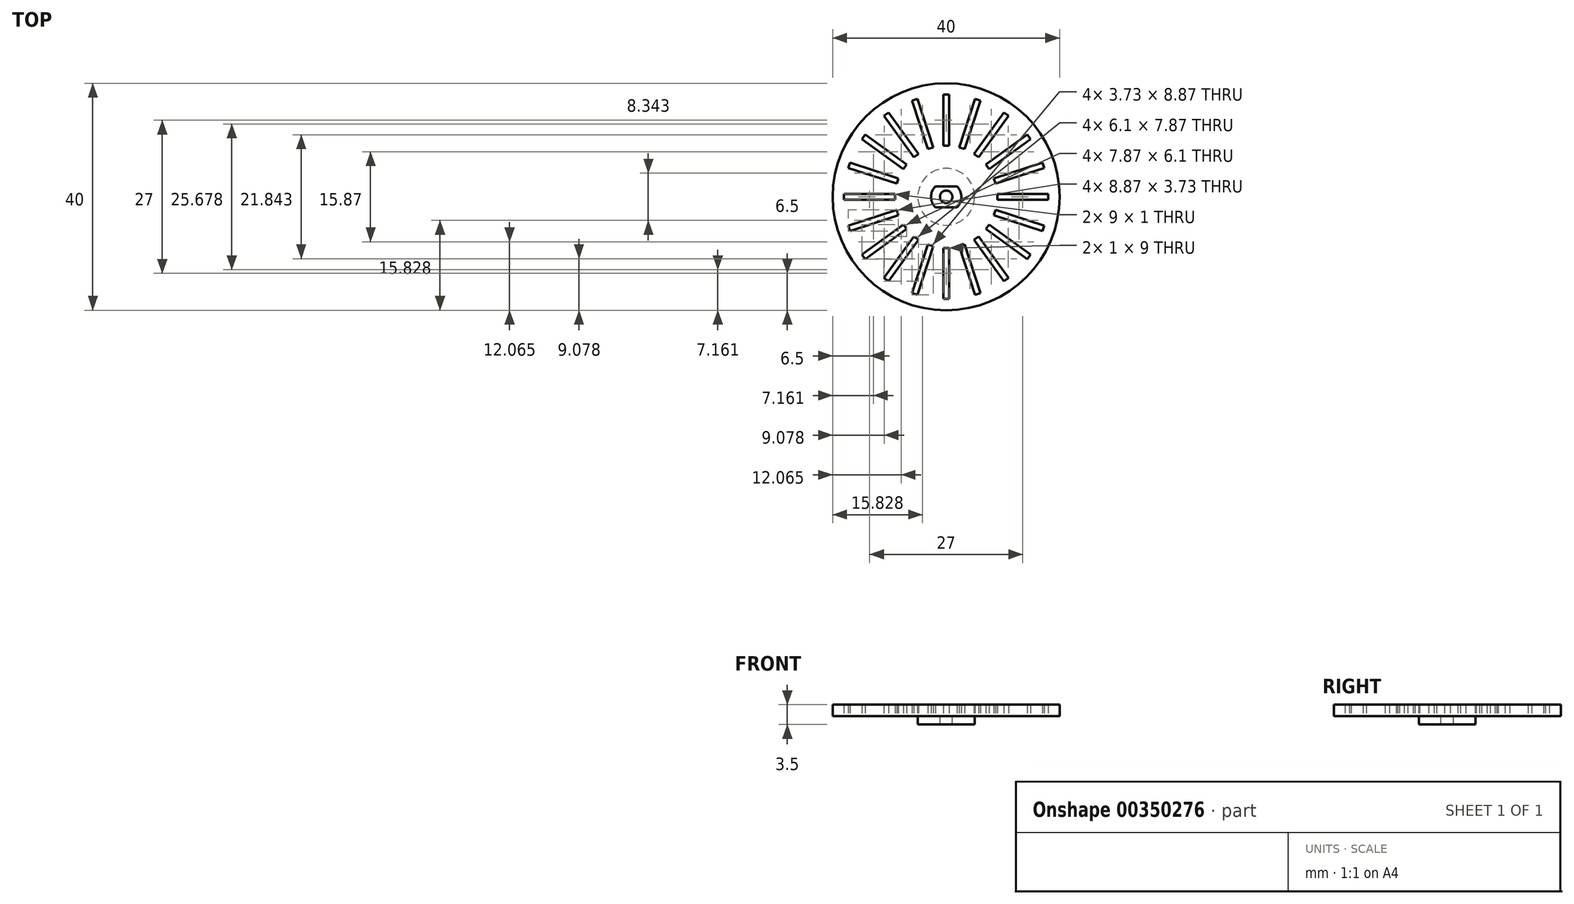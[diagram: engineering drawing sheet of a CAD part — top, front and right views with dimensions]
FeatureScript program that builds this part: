
annotation { "Feature Type Name" : "Feature", "Feature Type Description" : "" }
export const myFeature = defineFeature(function(context is Context, id is Id, definition is map)
    precondition{}
    {
        {
            var Q0;
            Q0=qCreatedBy(makeId("Top.planeOp"),FACE);
            var sketch = newSketch(context, id + "F0", { "sketchPlane" : qUnion([Q0])});
            skCircle(sketch, "E0", {"center": v(0, 0) * mm, "radius": 20 * mm});
            skArc(sketch, "E1", {"start": v(-1.9, 1.86) * mm, "mid": v(-2.67, 0) * mm, "end": v(-1.9, -1.86) * mm});
            skLineSegment(sketch, "E2.MirrorCS", {"start": v(-1.9, -1.86) * mm, "end": v(1.9, -1.86) * mm});
            skArc(sketch, "E3.trimOffspring", {"start": v(1.9, -1.86) * mm, "mid": v(2.67, 0) * mm, "end": v(1.9, 1.86) * mm});
            skLineSegment(sketch, "E4.MirrorCS", {"start": v(-1.9, 1.86) * mm, "end": v(1.9, 1.86) * mm});
            skLineSegment(sketch, "E5", {"start": v(0, -9) * mm, "end": v(-0.5, -9) * mm});
            skLineSegment(sketch, "E6", {"start": v(-0.5, -9) * mm, "end": v(-0.5, -18) * mm});
            skLineSegment(sketch, "E7", {"start": v(-0.5, -18) * mm, "end": v(0, -18) * mm});
            skLineSegment(sketch, "E8.MirrorCS", {"start": v(0.5, -9) * mm, "end": v(0.5, -18) * mm});
            skLineSegment(sketch, "E9", {"start": v(0, -9) * mm, "end": v(0.5, -9) * mm});
            skLineSegment(sketch, "E10", {"start": v(0, -18) * mm, "end": v(0.5, -18) * mm});
            skLineSegment(sketch, "E11.1.0", {"start": v(2.3, -8.71) * mm, "end": v(5.09, -17.27) * mm});
            skLineSegment(sketch, "E11.1.1", {"start": v(3.26, -8.4) * mm, "end": v(6.04, -16.96) * mm});
            skLineSegment(sketch, "E11.1.2", {"start": v(5.09, -17.27) * mm, "end": v(5.56, -17.12) * mm});
            skLineSegment(sketch, "E11.1.3", {"start": v(2.78, -8.56) * mm, "end": v(3.26, -8.4) * mm});
            skLineSegment(sketch, "E11.1.4", {"start": v(5.56, -17.12) * mm, "end": v(6.04, -16.96) * mm});
            skLineSegment(sketch, "E11.1.5", {"start": v(2.78, -8.56) * mm, "end": v(2.3, -8.71) * mm});
            skLineSegment(sketch, "E11.2.0", {"start": v(4.89, -7.58) * mm, "end": v(10.18, -14.86) * mm});
            skLineSegment(sketch, "E11.2.1", {"start": v(5.7, -6.99) * mm, "end": v(10.98, -14.27) * mm});
            skLineSegment(sketch, "E11.2.2", {"start": v(10.18, -14.86) * mm, "end": v(10.58, -14.56) * mm});
            skLineSegment(sketch, "E11.2.3", {"start": v(5.3, -7.28) * mm, "end": v(5.7, -6.99) * mm});
            skLineSegment(sketch, "E11.2.4", {"start": v(10.58, -14.56) * mm, "end": v(10.98, -14.27) * mm});
            skLineSegment(sketch, "E11.2.5", {"start": v(5.3, -7.28) * mm, "end": v(4.89, -7.58) * mm});
            skLineSegment(sketch, "E11.3.0", {"start": v(6.99, -5.7) * mm, "end": v(14.27, -10.98) * mm});
            skLineSegment(sketch, "E11.3.1", {"start": v(7.58, -4.89) * mm, "end": v(14.86, -10.18) * mm});
            skLineSegment(sketch, "E11.3.2", {"start": v(14.27, -10.98) * mm, "end": v(14.56, -10.58) * mm});
            skLineSegment(sketch, "E11.3.3", {"start": v(7.28, -5.3) * mm, "end": v(7.58, -4.89) * mm});
            skLineSegment(sketch, "E11.3.4", {"start": v(14.56, -10.58) * mm, "end": v(14.86, -10.18) * mm});
            skLineSegment(sketch, "E11.3.5", {"start": v(7.28, -5.3) * mm, "end": v(6.99, -5.7) * mm});
            skLineSegment(sketch, "E11.4.0", {"start": v(8.4, -3.26) * mm, "end": v(16.96, -6.04) * mm});
            skLineSegment(sketch, "E11.4.1", {"start": v(8.71, -2.3) * mm, "end": v(17.27, -5.09) * mm});
            skLineSegment(sketch, "E11.4.2", {"start": v(16.96, -6.04) * mm, "end": v(17.12, -5.56) * mm});
            skLineSegment(sketch, "E11.4.3", {"start": v(8.56, -2.78) * mm, "end": v(8.71, -2.3) * mm});
            skLineSegment(sketch, "E11.4.4", {"start": v(17.12, -5.56) * mm, "end": v(17.27, -5.09) * mm});
            skLineSegment(sketch, "E11.4.5", {"start": v(8.56, -2.78) * mm, "end": v(8.4, -3.26) * mm});
            skLineSegment(sketch, "E11.5.0", {"start": v(9, -0.5) * mm, "end": v(18, -0.5) * mm});
            skLineSegment(sketch, "E11.5.1", {"start": v(9, 0.5) * mm, "end": v(18, 0.5) * mm});
            skLineSegment(sketch, "E11.5.2", {"start": v(18, -0.5) * mm, "end": v(18, 0) * mm});
            skLineSegment(sketch, "E11.5.3", {"start": v(9, 0) * mm, "end": v(9, 0.5) * mm});
            skLineSegment(sketch, "E11.5.4", {"start": v(18, 0) * mm, "end": v(18, 0.5) * mm});
            skLineSegment(sketch, "E11.5.5", {"start": v(9, 0) * mm, "end": v(9, -0.5) * mm});
            skLineSegment(sketch, "E11.6.0", {"start": v(8.71, 2.3) * mm, "end": v(17.27, 5.09) * mm});
            skLineSegment(sketch, "E11.6.1", {"start": v(8.4, 3.26) * mm, "end": v(16.96, 6.04) * mm});
            skLineSegment(sketch, "E11.6.2", {"start": v(17.27, 5.09) * mm, "end": v(17.12, 5.56) * mm});
            skLineSegment(sketch, "E11.6.3", {"start": v(8.56, 2.78) * mm, "end": v(8.4, 3.26) * mm});
            skLineSegment(sketch, "E11.6.4", {"start": v(17.12, 5.56) * mm, "end": v(16.96, 6.04) * mm});
            skLineSegment(sketch, "E11.6.5", {"start": v(8.56, 2.78) * mm, "end": v(8.71, 2.3) * mm});
            skLineSegment(sketch, "E11.7.0", {"start": v(7.58, 4.89) * mm, "end": v(14.86, 10.18) * mm});
            skLineSegment(sketch, "E11.7.1", {"start": v(6.99, 5.7) * mm, "end": v(14.27, 10.98) * mm});
            skLineSegment(sketch, "E11.7.2", {"start": v(14.86, 10.18) * mm, "end": v(14.56, 10.58) * mm});
            skLineSegment(sketch, "E11.7.3", {"start": v(7.28, 5.3) * mm, "end": v(6.99, 5.7) * mm});
            skLineSegment(sketch, "E11.7.4", {"start": v(14.56, 10.58) * mm, "end": v(14.27, 10.98) * mm});
            skLineSegment(sketch, "E11.7.5", {"start": v(7.28, 5.3) * mm, "end": v(7.58, 4.89) * mm});
            skLineSegment(sketch, "E11.8.0", {"start": v(5.7, 6.99) * mm, "end": v(10.98, 14.27) * mm});
            skLineSegment(sketch, "E11.8.1", {"start": v(4.89, 7.58) * mm, "end": v(10.18, 14.86) * mm});
            skLineSegment(sketch, "E11.8.2", {"start": v(10.98, 14.27) * mm, "end": v(10.58, 14.56) * mm});
            skLineSegment(sketch, "E11.8.3", {"start": v(5.3, 7.28) * mm, "end": v(4.89, 7.58) * mm});
            skLineSegment(sketch, "E11.8.4", {"start": v(10.58, 14.56) * mm, "end": v(10.18, 14.86) * mm});
            skLineSegment(sketch, "E11.8.5", {"start": v(5.3, 7.28) * mm, "end": v(5.7, 6.99) * mm});
            skLineSegment(sketch, "E11.9.0", {"start": v(3.26, 8.4) * mm, "end": v(6.04, 16.96) * mm});
            skLineSegment(sketch, "E11.9.1", {"start": v(2.3, 8.71) * mm, "end": v(5.09, 17.27) * mm});
            skLineSegment(sketch, "E11.9.2", {"start": v(6.04, 16.96) * mm, "end": v(5.56, 17.12) * mm});
            skLineSegment(sketch, "E11.9.3", {"start": v(2.78, 8.56) * mm, "end": v(2.3, 8.71) * mm});
            skLineSegment(sketch, "E11.9.4", {"start": v(5.56, 17.12) * mm, "end": v(5.09, 17.27) * mm});
            skLineSegment(sketch, "E11.9.5", {"start": v(2.78, 8.56) * mm, "end": v(3.26, 8.4) * mm});
            skLineSegment(sketch, "E11.10.0", {"start": v(0.5, 9) * mm, "end": v(0.5, 18) * mm});
            skLineSegment(sketch, "E11.10.1", {"start": v(-0.5, 9) * mm, "end": v(-0.5, 18) * mm});
            skLineSegment(sketch, "E11.10.2", {"start": v(0.5, 18) * mm, "end": v(0, 18) * mm});
            skLineSegment(sketch, "E11.10.3", {"start": v(0, 9) * mm, "end": v(-0.5, 9) * mm});
            skLineSegment(sketch, "E11.10.4", {"start": v(0, 18) * mm, "end": v(-0.5, 18) * mm});
            skLineSegment(sketch, "E11.10.5", {"start": v(0, 9) * mm, "end": v(0.5, 9) * mm});
            skLineSegment(sketch, "E11.11.0", {"start": v(-2.3, 8.71) * mm, "end": v(-5.09, 17.27) * mm});
            skLineSegment(sketch, "E11.11.1", {"start": v(-3.26, 8.4) * mm, "end": v(-6.04, 16.96) * mm});
            skLineSegment(sketch, "E11.11.2", {"start": v(-5.09, 17.27) * mm, "end": v(-5.56, 17.12) * mm});
            skLineSegment(sketch, "E11.11.3", {"start": v(-2.78, 8.56) * mm, "end": v(-3.26, 8.4) * mm});
            skLineSegment(sketch, "E11.11.4", {"start": v(-5.56, 17.12) * mm, "end": v(-6.04, 16.96) * mm});
            skLineSegment(sketch, "E11.11.5", {"start": v(-2.78, 8.56) * mm, "end": v(-2.3, 8.71) * mm});
            skLineSegment(sketch, "E11.12.0", {"start": v(-4.89, 7.58) * mm, "end": v(-10.18, 14.86) * mm});
            skLineSegment(sketch, "E11.12.1", {"start": v(-5.7, 6.99) * mm, "end": v(-10.98, 14.27) * mm});
            skLineSegment(sketch, "E11.12.2", {"start": v(-10.18, 14.86) * mm, "end": v(-10.58, 14.56) * mm});
            skLineSegment(sketch, "E11.12.3", {"start": v(-5.3, 7.28) * mm, "end": v(-5.7, 6.99) * mm});
            skLineSegment(sketch, "E11.12.4", {"start": v(-10.58, 14.56) * mm, "end": v(-10.98, 14.27) * mm});
            skLineSegment(sketch, "E11.12.5", {"start": v(-5.3, 7.28) * mm, "end": v(-4.89, 7.58) * mm});
            skLineSegment(sketch, "E11.13.0", {"start": v(-6.99, 5.7) * mm, "end": v(-14.27, 10.98) * mm});
            skLineSegment(sketch, "E11.13.1", {"start": v(-7.58, 4.89) * mm, "end": v(-14.86, 10.18) * mm});
            skLineSegment(sketch, "E11.13.2", {"start": v(-14.27, 10.98) * mm, "end": v(-14.56, 10.58) * mm});
            skLineSegment(sketch, "E11.13.3", {"start": v(-7.28, 5.3) * mm, "end": v(-7.58, 4.89) * mm});
            skLineSegment(sketch, "E11.13.4", {"start": v(-14.56, 10.58) * mm, "end": v(-14.86, 10.18) * mm});
            skLineSegment(sketch, "E11.13.5", {"start": v(-7.28, 5.3) * mm, "end": v(-6.99, 5.7) * mm});
            skLineSegment(sketch, "E11.14.0", {"start": v(-8.4, 3.26) * mm, "end": v(-16.96, 6.04) * mm});
            skLineSegment(sketch, "E11.14.1", {"start": v(-8.71, 2.3) * mm, "end": v(-17.27, 5.09) * mm});
            skLineSegment(sketch, "E11.14.2", {"start": v(-16.96, 6.04) * mm, "end": v(-17.12, 5.56) * mm});
            skLineSegment(sketch, "E11.14.3", {"start": v(-8.56, 2.78) * mm, "end": v(-8.71, 2.3) * mm});
            skLineSegment(sketch, "E11.14.4", {"start": v(-17.12, 5.56) * mm, "end": v(-17.27, 5.09) * mm});
            skLineSegment(sketch, "E11.14.5", {"start": v(-8.56, 2.78) * mm, "end": v(-8.4, 3.26) * mm});
            skLineSegment(sketch, "E11.15.0", {"start": v(-9, 0.5) * mm, "end": v(-18, 0.5) * mm});
            skLineSegment(sketch, "E11.15.1", {"start": v(-9, -0.5) * mm, "end": v(-18, -0.5) * mm});
            skLineSegment(sketch, "E11.15.2", {"start": v(-18, 0.5) * mm, "end": v(-18, 0) * mm});
            skLineSegment(sketch, "E11.15.3", {"start": v(-9, 0) * mm, "end": v(-9, -0.5) * mm});
            skLineSegment(sketch, "E11.15.4", {"start": v(-18, 0) * mm, "end": v(-18, -0.5) * mm});
            skLineSegment(sketch, "E11.15.5", {"start": v(-9, 0) * mm, "end": v(-9, 0.5) * mm});
            skLineSegment(sketch, "E11.16.0", {"start": v(-8.71, -2.3) * mm, "end": v(-17.27, -5.09) * mm});
            skLineSegment(sketch, "E11.16.1", {"start": v(-8.4, -3.26) * mm, "end": v(-16.96, -6.04) * mm});
            skLineSegment(sketch, "E11.16.2", {"start": v(-17.27, -5.09) * mm, "end": v(-17.12, -5.56) * mm});
            skLineSegment(sketch, "E11.16.3", {"start": v(-8.56, -2.78) * mm, "end": v(-8.4, -3.26) * mm});
            skLineSegment(sketch, "E11.16.4", {"start": v(-17.12, -5.56) * mm, "end": v(-16.96, -6.04) * mm});
            skLineSegment(sketch, "E11.16.5", {"start": v(-8.56, -2.78) * mm, "end": v(-8.71, -2.3) * mm});
            skLineSegment(sketch, "E11.17.0", {"start": v(-7.58, -4.89) * mm, "end": v(-14.86, -10.18) * mm});
            skLineSegment(sketch, "E11.17.1", {"start": v(-6.99, -5.7) * mm, "end": v(-14.27, -10.98) * mm});
            skLineSegment(sketch, "E11.17.2", {"start": v(-14.86, -10.18) * mm, "end": v(-14.56, -10.58) * mm});
            skLineSegment(sketch, "E11.17.3", {"start": v(-7.28, -5.3) * mm, "end": v(-6.99, -5.7) * mm});
            skLineSegment(sketch, "E11.17.4", {"start": v(-14.56, -10.58) * mm, "end": v(-14.27, -10.98) * mm});
            skLineSegment(sketch, "E11.17.5", {"start": v(-7.28, -5.3) * mm, "end": v(-7.58, -4.89) * mm});
            skLineSegment(sketch, "E11.18.0", {"start": v(-5.7, -6.99) * mm, "end": v(-10.98, -14.27) * mm});
            skLineSegment(sketch, "E11.18.1", {"start": v(-4.89, -7.58) * mm, "end": v(-10.18, -14.86) * mm});
            skLineSegment(sketch, "E11.18.2", {"start": v(-10.98, -14.27) * mm, "end": v(-10.58, -14.56) * mm});
            skLineSegment(sketch, "E11.18.3", {"start": v(-5.3, -7.28) * mm, "end": v(-4.89, -7.58) * mm});
            skLineSegment(sketch, "E11.18.4", {"start": v(-10.58, -14.56) * mm, "end": v(-10.18, -14.86) * mm});
            skLineSegment(sketch, "E11.18.5", {"start": v(-5.3, -7.28) * mm, "end": v(-5.7, -6.99) * mm});
            skLineSegment(sketch, "E11.19.0", {"start": v(-3.26, -8.4) * mm, "end": v(-6.04, -16.96) * mm});
            skLineSegment(sketch, "E11.19.1", {"start": v(-2.3, -8.71) * mm, "end": v(-5.09, -17.27) * mm});
            skLineSegment(sketch, "E11.19.2", {"start": v(-6.04, -16.96) * mm, "end": v(-5.56, -17.12) * mm});
            skLineSegment(sketch, "E11.19.3", {"start": v(-2.78, -8.56) * mm, "end": v(-2.3, -8.71) * mm});
            skLineSegment(sketch, "E11.19.4", {"start": v(-5.56, -17.12) * mm, "end": v(-5.09, -17.27) * mm});
            skLineSegment(sketch, "E11.19.5", {"start": v(-2.78, -8.56) * mm, "end": v(-3.26, -8.4) * mm});
            skSolve(sketch);
        }
        {
            var Q0;
            Q0 = qSketchRegion(id + "F0", true);
            var Q1;
            Q1=makeQuery(id+"F0.imprint","IMPRINT",FACE,{"disambiguationData":[TD([[makeQuery(id+"F0.imprint","IMPRINT",EDGE,{"derivedFrom":sQuery(id+"F0.wireOp",EDGE,"E0")}),1.0]])]});
            extrude(context, id + "F1", {"entities" : qUnion([Q0, Q1]), "depth" : 2 * mm});
        }
        {
            var Q0;
            Q0=qCreatedBy(makeId("Top.planeOp"),FACE);
            var sketch = newSketch(context, id + "F2", { "sketchPlane" : qUnion([Q0])});
            skCircle(sketch, "E12", {"center": v(0, 0) * mm, "radius": 5 * mm});
            skCircle(sketch, "E13", {"center": v(0, 0) * mm, "radius": 1.1 * mm});
            skSolve(sketch);
        }
        {
            var Q0;
            Q0 = qSketchRegion(id + "F2", true);
            extrude(context, id + "F3", {"entities" : qUnion([Q0]), "operationType" : NewBodyOperationType.ADD, "oppositeDirection" : true, "depth" : 1.5 * mm});
        }
    });
